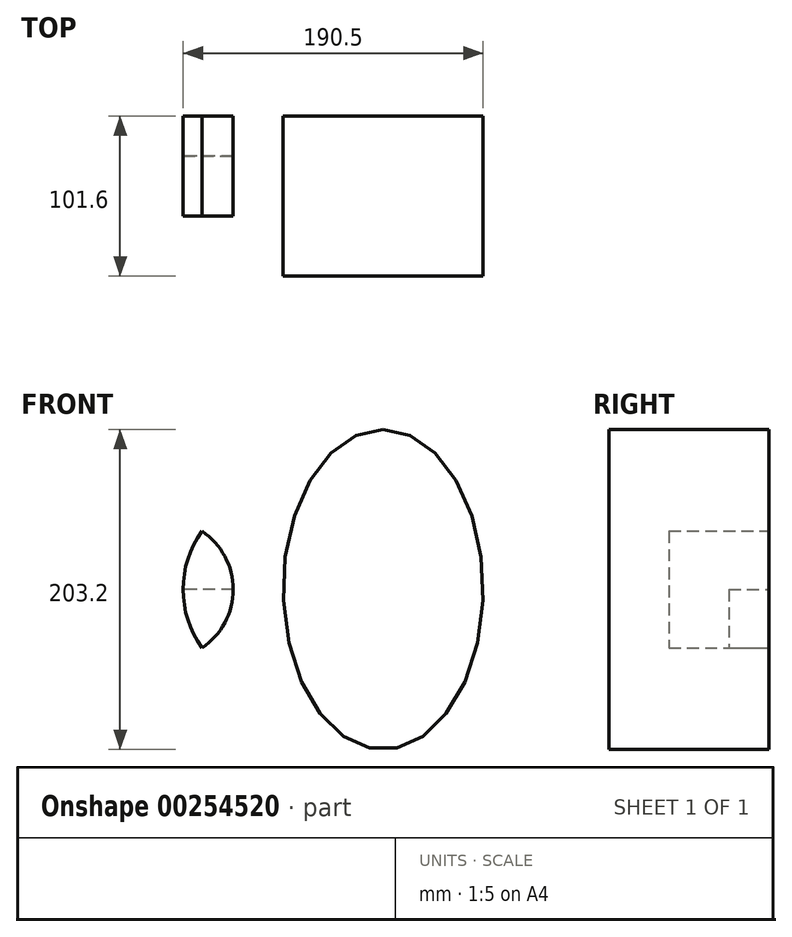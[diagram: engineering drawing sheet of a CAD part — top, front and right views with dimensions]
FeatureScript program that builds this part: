
annotation { "Feature Type Name" : "Feature", "Feature Type Description" : "" }
export const myFeature = defineFeature(function(context is Context, id is Id, definition is map)
    precondition{}
    {
        {
            var Q0;
            Q0=qCreatedBy(makeId("Front.planeOp"),FACE);
            var sketch = newSketch(context, id + "F0", { "sketchPlane" : qUnion([Q0])});
            skLineSegment(sketch, "E0", {"start": v(0, 0) * mm, "end": v(-76.2, 0) * mm});
            skCircle(sketch, "E1", {"center": v(-76.2, 0) * mm, "radius": 44.45 * mm});
            skLineSegment(sketch, "E2", {"start": v(-31.75, 0) * mm, "end": v(-63.5, 0) * mm});
            skCircle(sketch, "E3", {"center": v(0, 0) * mm, "radius": 63.5 * mm});
            skEllipse(sketch, "E4", {"center": v(63.5, 0) * mm, "majorRadius": 101.6 * mm, "minorRadius": 63.5 * mm, "majorAxis": v(0, 1)});
            skSolve(sketch);
        }
        {
            var Q0;
            {var subQ0=sQuery(id+"F0.wireOp",EDGE,"E3");var subQ1=sQuery(id+"F0.wireOp",EDGE,"E1");var subQ2=makeQuery(id+"F0.imprint","INTERSECT",VERTEX,{"disambiguationData":[OD(0.0)],"derivedFrom":[subQ1,subQ0]});Q0=makeQuery(id+"F0.imprint","IMPRINT",FACE,{"disambiguationData":[TD([[makeQuery(id+"F0.imprint","IMPRINT",EDGE,{"disambiguationData":[TD([[subQ2,-1.0]])],"derivedFrom":subQ1}),1.0]])]});}
            extrude(context, id + "F1", {"entities" : qUnion([Q0]), "depth" : 25.4 * mm});
        }
        {
            var Q0;
            {var subQ3=sQuery(id+"F0.wireOp",EDGE,"E1");var subQ5=sQuery(id+"F0.wireOp",EDGE,"E3");var subQ6=makeQuery(id+"F0.imprint","INTERSECT",VERTEX,{"disambiguationData":[OD(1.0)],"derivedFrom":[subQ3,subQ5]});Q0=makeQuery(id+"F0.imprint","IMPRINT",FACE,{"disambiguationData":[TD([[makeQuery(id+"F0.imprint","IMPRINT",EDGE,{"disambiguationData":[TD([[subQ6,-1.0]])],"derivedFrom":subQ5}),1.0]])]});}
            var Q1;
            {var subQ3=sQuery(id+"F0.wireOp",EDGE,"E1");var subQ5=sQuery(id+"F0.wireOp",EDGE,"E3");var subQ6=makeQuery(id+"F0.imprint","INTERSECT",VERTEX,{"disambiguationData":[OD(0.0)],"derivedFrom":[subQ3,subQ5]});Q1=makeQuery(id+"F0.imprint","IMPRINT",FACE,{"disambiguationData":[TD([[makeQuery(id+"F0.imprint","IMPRINT",EDGE,{"disambiguationData":[TD([[subQ6,1.0]])],"derivedFrom":subQ5}),1.0]])]});}
            var Q2;
            {var subQ0=sQuery(id+"F0.wireOp",EDGE,"E2");Q2=makeQuery(id+"F0.imprint","IMPRINT",FACE,{"disambiguationData":[TD([[makeQuery(id+"F0.imprint","IMPRINT",EDGE,{"derivedFrom":subQ0}),1.0]])]});}
            var Q3;
            {var subQ0=sQuery(id+"F0.wireOp",EDGE,"E2");Q3=makeQuery(id+"F0.imprint","IMPRINT",FACE,{"disambiguationData":[TD([[makeQuery(id+"F0.imprint","IMPRINT",EDGE,{"derivedFrom":subQ0}),-1.0]])]});}
            extrude(context, id + "F2", {"entities" : qUnion([Q0, Q1, Q2, Q3]), "depth" : 63.5 * mm});
        }
        {
            var Q0;
            {var subQ0=sQuery(id+"F0.wireOp",EDGE,"E4");var subQ1=sQuery(id+"F0.wireOp",EDGE,"E3");var subQ2=makeQuery(id+"F0.imprint","INTERSECT",VERTEX,{"disambiguationData":[OD(0.0)],"derivedFrom":[subQ1,subQ0]});Q0=makeQuery(id+"F0.imprint","IMPRINT",FACE,{"disambiguationData":[TD([[makeQuery(id+"F0.imprint","IMPRINT",EDGE,{"disambiguationData":[TD([[subQ2,1.0]])],"derivedFrom":subQ1}),-1.0]])]});}
            var Q1;
            {var subQ0=sQuery(id+"F0.wireOp",EDGE,"E4");var subQ1=sQuery(id+"F0.wireOp",EDGE,"E3");var subQ2=makeQuery(id+"F0.imprint","INTERSECT",VERTEX,{"disambiguationData":[OD(0.0)],"derivedFrom":[subQ1,subQ0]});Q1=makeQuery(id+"F0.imprint","IMPRINT",FACE,{"disambiguationData":[TD([[makeQuery(id+"F0.imprint","IMPRINT",EDGE,{"disambiguationData":[TD([[subQ2,1.0]])],"derivedFrom":subQ1}),1.0]])]});}
            extrude(context, id + "F3", {"entities" : qUnion([Q0, Q1]), "depth" : 101.6 * mm});
        }
    });
